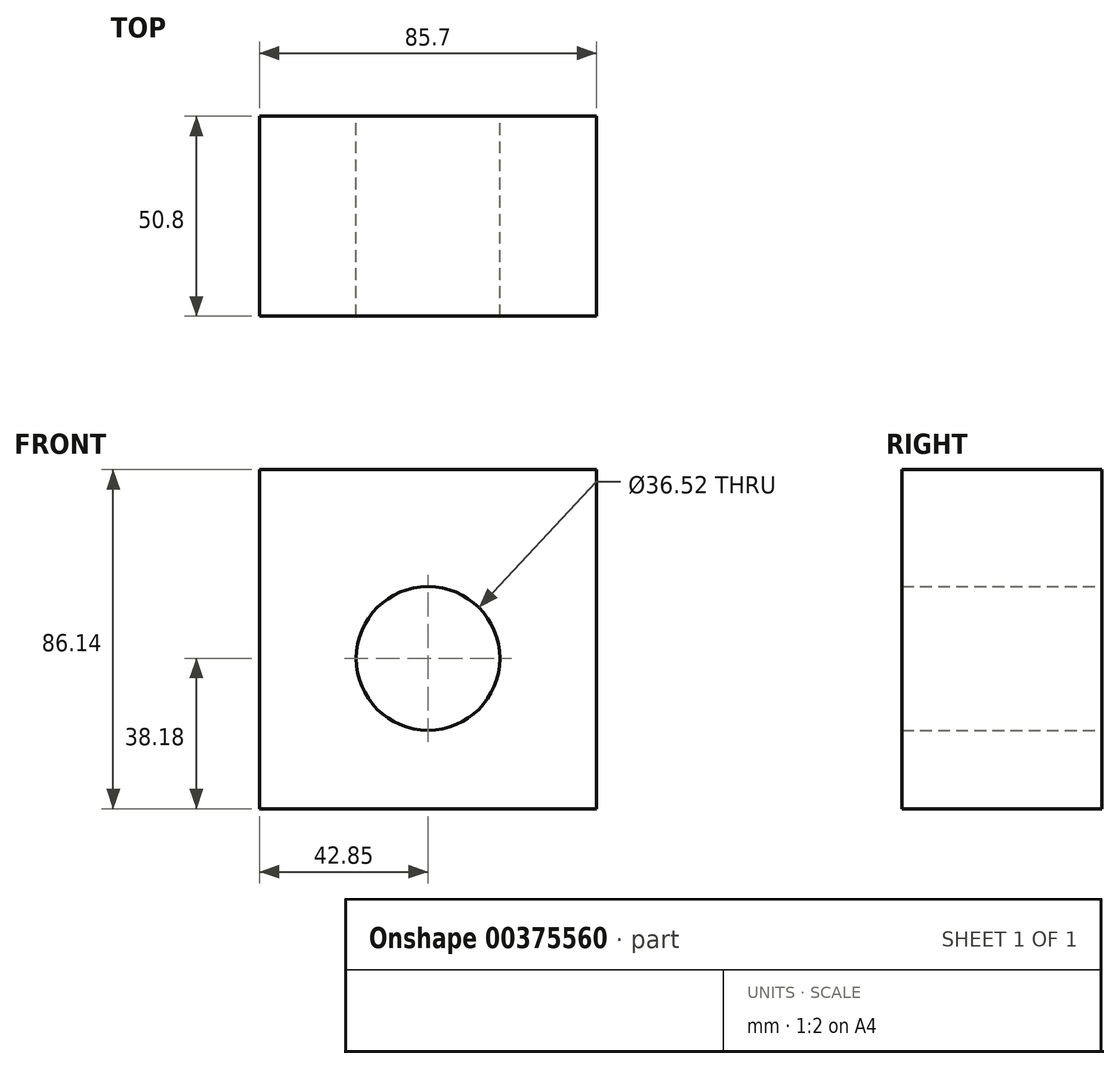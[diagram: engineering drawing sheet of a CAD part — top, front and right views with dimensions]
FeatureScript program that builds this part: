
annotation { "Feature Type Name" : "Feature", "Feature Type Description" : "" }
export const myFeature = defineFeature(function(context is Context, id is Id, definition is map)
    precondition{}
    {
        {
            var Q0;
            Q0=qCreatedBy(makeId("Front.planeOp"),FACE);
            var sketch = newSketch(context, id + "F0", { "sketchPlane" : qUnion([Q0])});
            skLineSegment(sketch, "E0.bottom", {"start": v(-42.85, 47.96) * mm, "end": v(42.85, 47.96) * mm});
            skLineSegment(sketch, "E0.top", {"start": v(-42.85, -38.18) * mm, "end": v(42.85, -38.18) * mm});
            skLineSegment(sketch, "E0.left", {"start": v(-42.85, 47.96) * mm, "end": v(-42.85, -38.18) * mm});
            skLineSegment(sketch, "E0.right", {"start": v(42.85, 47.96) * mm, "end": v(42.85, -38.18) * mm});
            skSolve(sketch);
        }
        {
            var Q0;
            Q0 = qSketchRegion(id + "F0", true);
            extrude(context, id + "F1", {"entities" : qUnion([Q0]), "depth" : 25.4 * mm});
        }
        {
            var Q0;
            Q0=qCreatedBy(makeId("Front.planeOp"),FACE);
            var sketch = newSketch(context, id + "F2", { "sketchPlane" : qUnion([Q0])});
            skCircle(sketch, "E1", {"center": v(0, 0) * mm, "radius": 18.26 * mm});
            skSolve(sketch);
        }
        {
            var Q0;
            Q0=makeQuery(id+"F2.imprint","IMPRINT",FACE,{"disambiguationData":[TD([[makeQuery(id+"F2.imprint","IMPRINT",EDGE,{"derivedFrom":sQuery(id+"F2.wireOp",EDGE,"E1")}),1.0]])]});
            extrude(context, id + "F3", {"entities" : qUnion([Q0]), "operationType" : NewBodyOperationType.REMOVE, "depth" : 162.21 * mm});
        }
        {
            var Q0;
            Q0=makeQuery(id+"F1.opExtrude","CAP_FACE",FACE,{"disambiguationData":[OSD([sQuery(id+"F0.wireOp",EDGE,"E0.bottom"),sQuery(id+"F0.wireOp",EDGE,"E0.top"),sQuery(id+"F0.wireOp",EDGE,"E0.left"),sQuery(id+"F0.wireOp",EDGE,"E0.right")])],"isStart":false});
            extrude(context, id + "F4", {"entities" : qUnion([Q0]), "operationType" : NewBodyOperationType.ADD, "depth" : 25.4 * mm});
        }
    });
